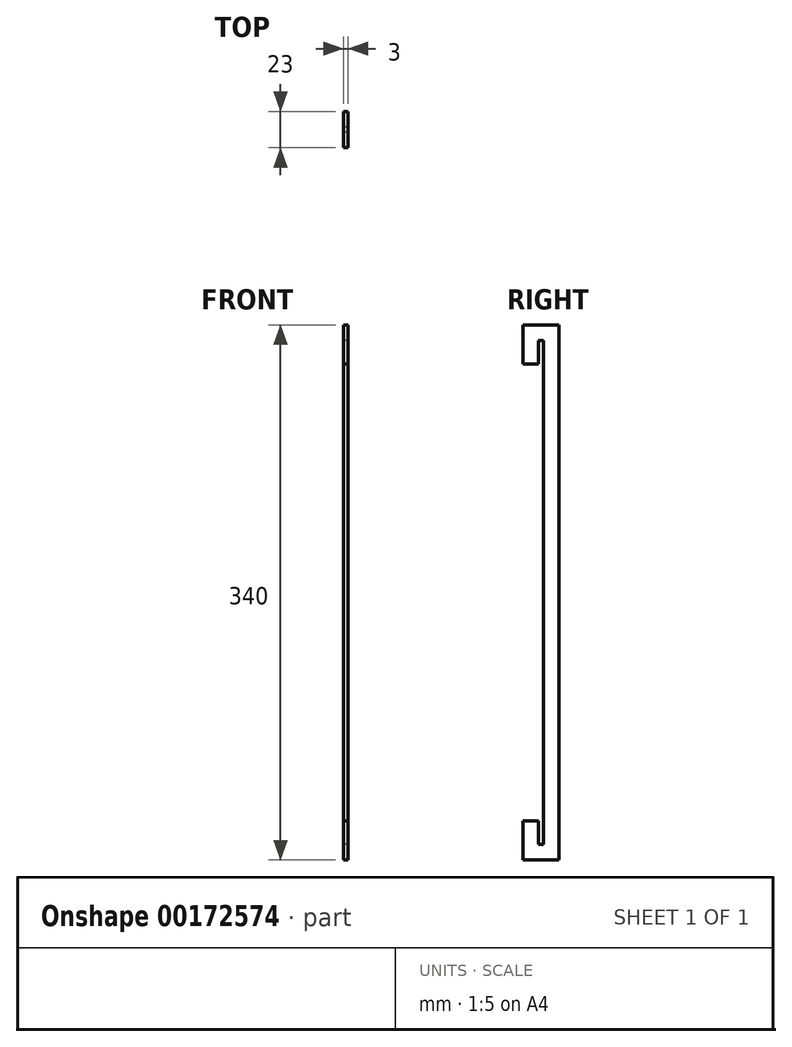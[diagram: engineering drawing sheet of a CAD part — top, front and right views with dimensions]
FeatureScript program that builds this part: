
annotation { "Feature Type Name" : "Feature", "Feature Type Description" : "" }
export const myFeature = defineFeature(function(context is Context, id is Id, definition is map)
    precondition{}
    {
        {
            var Q0;
            Q0=qCreatedBy(makeId("Right.planeOp"),FACE);
            var sketch = newSketch(context, id + "F0", { "sketchPlane" : qUnion([Q0])});
            skLineSegment(sketch, "E0", {"start": v(0, 0) * mm, "end": v(0, -25) * mm});
            skLineSegment(sketch, "E1", {"start": v(0, -25) * mm, "end": v(23, -25) * mm});
            skLineSegment(sketch, "E2", {"start": v(23, -25) * mm, "end": v(23, 315) * mm});
            skLineSegment(sketch, "E3", {"start": v(23, 315) * mm, "end": v(0, 315) * mm});
            skLineSegment(sketch, "E4", {"start": v(0, 315) * mm, "end": v(0, 290) * mm});
            skLineSegment(sketch, "E5", {"start": v(0, 290) * mm, "end": v(10, 290) * mm});
            skLineSegment(sketch, "E6", {"start": v(10, 290) * mm, "end": v(10, 305) * mm});
            skLineSegment(sketch, "E7", {"start": v(10, 305) * mm, "end": v(13, 305) * mm});
            skLineSegment(sketch, "E8", {"start": v(13, 305) * mm, "end": v(13, -15) * mm});
            skLineSegment(sketch, "E9", {"start": v(13, -15) * mm, "end": v(10, -15) * mm});
            skLineSegment(sketch, "E10", {"start": v(10, -15) * mm, "end": v(10, 0) * mm});
            skLineSegment(sketch, "E11", {"start": v(10, 0) * mm, "end": v(0, 0) * mm});
            skSolve(sketch);
        }
        {
            var Q0;
            Q0 = qSketchRegion(id + "F0", true);
            extrude(context, id + "F1", {"entities" : qUnion([Q0]), "depth" : 3 * mm, "offsetDistance" : 25 * mm});
        }
    });
